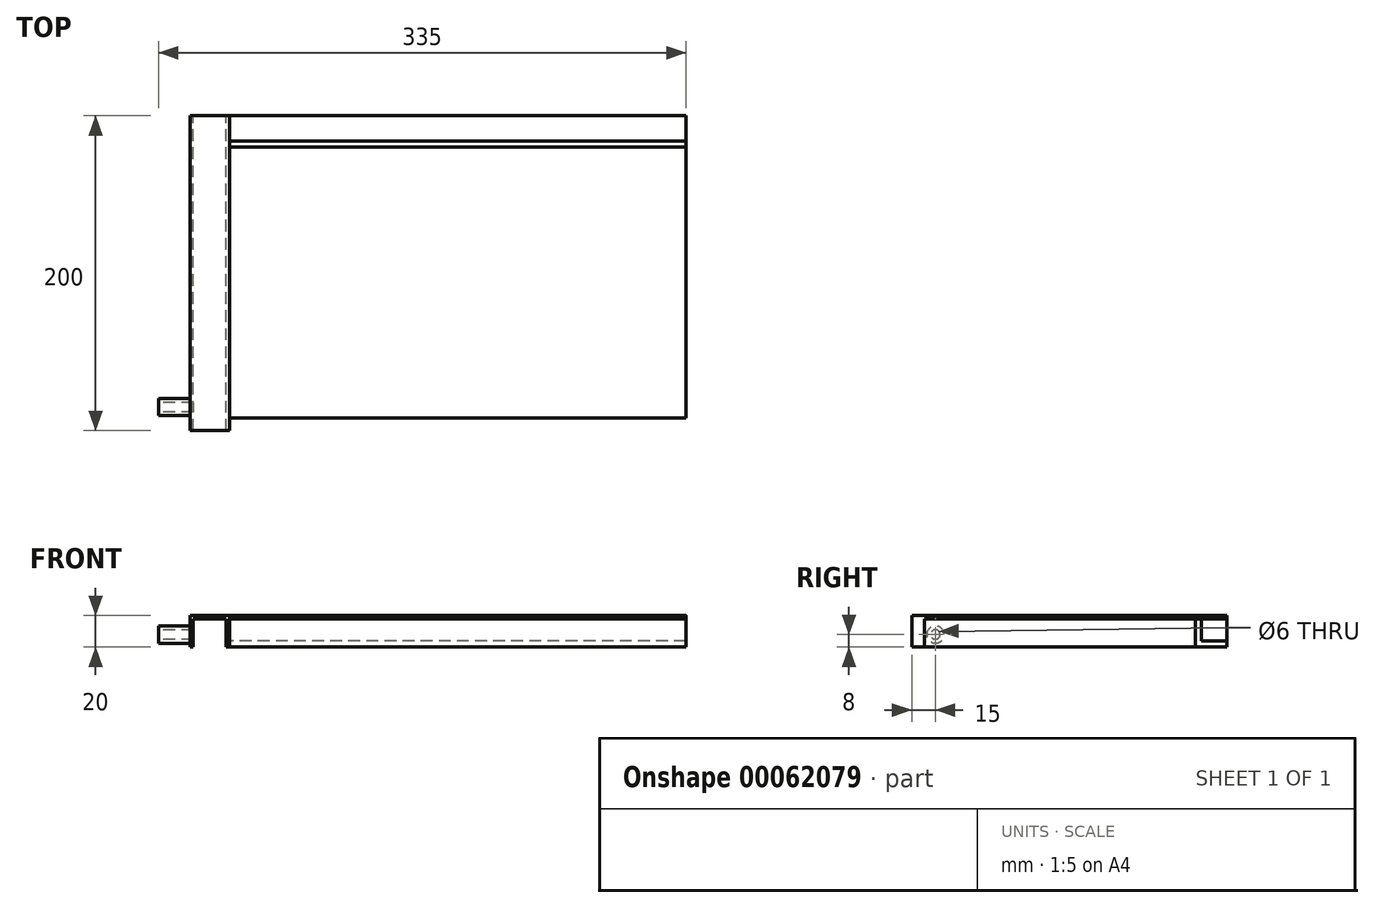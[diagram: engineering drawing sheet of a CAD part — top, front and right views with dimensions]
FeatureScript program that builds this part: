
annotation { "Feature Type Name" : "Feature", "Feature Type Description" : "" }
export const myFeature = defineFeature(function(context is Context, id is Id, definition is map)
    precondition{}
    {
        {
            assignVariable(context, id + "F0", {"name" : "l", "anyValue" : 200});
        }
        {
            assignVariable(context, id + "F1", {"name" : "w", "anyValue" : 294});
        }
        {
            var Q0;
            Q0=qCreatedBy(makeId("Front.planeOp"),FACE);
            var sketch = newSketch(context, id + "F2", { "sketchPlane" : qUnion([Q0])});
            skLineSegment(sketch, "E0.bottom", {"start": v(0, 0) * mm, "end": v(-2, 0) * mm});
            skLineSegment(sketch, "E0.top", {"start": v(0, 20) * mm, "end": v(-25, 20) * mm});
            skLineSegment(sketch, "E0.left", {"start": v(0, 0) * mm, "end": v(0, 20) * mm});
            skLineSegment(sketch, "E0.right", {"start": v(-25, 0) * mm, "end": v(-25, 20) * mm});
            skLineSegment(sketch, "E1.top", {"start": v(-2, 18) * mm, "end": v(-23, 18) * mm});
            skLineSegment(sketch, "E1.left", {"start": v(-2, 0) * mm, "end": v(-2, 18) * mm});
            skLineSegment(sketch, "E1.right", {"start": v(-23, 0) * mm, "end": v(-23, 18) * mm});
            skLineSegment(sketch, "E2", {"start": v(-23, 0) * mm, "end": v(-25, 0) * mm});
            skLineSegment(sketch, "E3", {"start": v(-23, 18) * mm, "end": v(-23, 20) * mm, "construction": true});
            skSolve(sketch);
        }
        {
            var Q0;
            Q0=makeQuery(id+"F2.imprint","IMPRINT",FACE,{"disambiguationData":[TD([[makeQuery(id+"F2.imprint","IMPRINT",EDGE,{"derivedFrom":sQuery(id+"F2.wireOp",EDGE,"E0.bottom")}),-1.0]])]});
            extrude(context, id + "F3", {"entities" : qUnion([Q0]), "depth" : (getVariable(context, 'l')) * mm});
        }
        {
            var Q0;
            Q0 = qSketchRegion(id + "F2", true);
            extrude(context, id + "F4", {"entities" : qUnion([Q0]), "depth" : (getVariable(context, 'l')) * mm});
        }
        {
            var Q0;
            Q0=makeQuery(id+"F4.opExtrude","SWEPT_FACE",FACE,{"disambiguationData":[OSD([sQuery(id+"F2.wireOp",EDGE,"E0.right")])]});
            var sketch = newSketch(context, id + "F5", { "sketchPlane" : qUnion([Q0])});
            skCircle(sketch, "E4", {"center": v(185, 8) * mm, "radius": 5.5 * mm});
            skSolve(sketch);
        }
        {
            var Q0;
            Q0=makeQuery(id+"F5.imprint","IMPRINT",FACE,{"disambiguationData":[TD([[makeQuery(id+"F5.imprint","IMPRINT",EDGE,{"derivedFrom":sQuery(id+"F5.wireOp",EDGE,"E4")}),1.0]])]});
            extrude(context, id + "F6", {"entities" : qUnion([Q0]), "operationType" : NewBodyOperationType.ADD, "depth" : 20 * mm});
        }
        {
            var Q0;
            Q0=makeQuery(id+"F6.opExtrude","CAP_FACE",FACE,{"disambiguationData":[OSD([sQuery(id+"F5.wireOp",EDGE,"E4")])],"isStart":false});
            var sketch = newSketch(context, id + "F7", { "sketchPlane" : qUnion([Q0])});
            skCircle(sketch, "E5", {"center": v(185, 8) * mm, "radius": 3 * mm});
            skSolve(sketch);
        }
        {
            var Q0;
            Q0=makeQuery(id+"F7.imprint","IMPRINT",FACE,{"disambiguationData":[TD([[makeQuery(id+"F7.imprint","IMPRINT",EDGE,{"derivedFrom":sQuery(id+"F7.wireOp",EDGE,"E5")}),1.0]])]});
            extrude(context, id + "F8", {"entities" : qUnion([Q0]), "operationType" : NewBodyOperationType.REMOVE, "oppositeDirection" : true, "depth" : 35 * mm});
        }
        {
            var Q0;
            Q0=qCreatedBy(makeId("Right.planeOp"),FACE);
            var sketch = newSketch(context, id + "F9", { "sketchPlane" : qUnion([Q0])});
            skLineSegment(sketch, "E6.bottom", {"start": v(0, 0) * mm, "end": v(-20, 0) * mm});
            skLineSegment(sketch, "E6.right", {"start": v(-20, 0) * mm, "end": v(-20, 20) * mm});
            skLineSegment(sketch, "E7.top", {"start": v(0, 4) * mm, "end": v(-16, 4) * mm});
            skLineSegment(sketch, "E7.right", {"start": v(-16, 20) * mm, "end": v(-16, 4) * mm});
            skLineSegment(sketch, "E8", {"start": v(-16, 20) * mm, "end": v(-20, 20) * mm});
            skLineSegment(sketch, "E9", {"start": v(0, 4) * mm, "end": v(0, 4) * mm});
            skLineSegment(sketch, "E10", {"start": v(0, 0) * mm, "end": v(0, 4) * mm});
            skSolve(sketch);
        }
        {
            var Q0;
            Q0=makeQuery(id+"F9.imprint","IMPRINT",FACE,{"disambiguationData":[TD([[makeQuery(id+"F9.imprint","IMPRINT",EDGE,{"derivedFrom":sQuery(id+"F9.wireOp",EDGE,"E6.bottom")}),-1.0]])]});
            extrude(context, id + "F10", {"entities" : qUnion([Q0]), "depth" : (getVariable(context, 'w') - 4) * mm});
        }
        {
            var Q0;
            Q0=makeQuery(id+"F10.opExtrude","SWEPT_EDGE",EDGE,{"disambiguationData":[OSD([sQuery(id+"F9.wireOp",EDGE,"E7.right"),sQuery(id+"F9.wireOp",EDGE,"E8")])]});
            var Q1;
            Q1=makeQuery(id+"F10.opExtrude","SWEPT_EDGE",EDGE,{"disambiguationData":[OSD([sQuery(id+"F9.wireOp",EDGE,"E7.top"),sQuery(id+"F9.wireOp",EDGE,"E10")])]});
            var Q2;
            Q2=makeQuery(id+"F10.opExtrude","SWEPT_EDGE",EDGE,{"disambiguationData":[OSD([sQuery(id+"F9.wireOp",EDGE,"E6.bottom"),sQuery(id+"F9.wireOp",EDGE,"E10")])]});
            var Q3;
            Q3=makeQuery(id+"F10.opExtrude","SWEPT_EDGE",EDGE,{"disambiguationData":[OSD([sQuery(id+"F9.wireOp",EDGE,"E6.bottom"),sQuery(id+"F9.wireOp",EDGE,"E6.right")])]});
            var Q4;
            Q4=makeQuery(id+"F10.opExtrude","SWEPT_EDGE",EDGE,{"disambiguationData":[OSD([sQuery(id+"F9.wireOp",EDGE,"E6.right"),sQuery(id+"F9.wireOp",EDGE,"E8")])]});
            fillet(context, id + "F11", {"entities" : qUnion([Q0, Q1, Q2, Q3, Q4]), "radius" : 1.5 * mm, "tangentPropagation" : true, "allowEdgeOverflow" : false});
        }
        {
            var Q0;
            Q0=qCreatedBy(makeId("Top.planeOp"),FACE);
            var sketch = newSketch(context, id + "F12", { "sketchPlane" : qUnion([Q0])});
            skLineSegment(sketch, "E11.bottom", {"start": v(0, 0) * mm, "end": v(290, 0) * mm});
            skLineSegment(sketch, "E11.top", {"start": v(0, -192) * mm, "end": v(290, -192) * mm});
            skLineSegment(sketch, "E11.left", {"start": v(0, 0) * mm, "end": v(0, -192) * mm});
            skLineSegment(sketch, "E11.right", {"start": v(290, 0) * mm, "end": v(290, -192) * mm});
            skSolve(sketch);
        }
        {
            var Q0;
            Q0=makeQuery(id+"F12.imprint","IMPRINT",FACE,{"disambiguationData":[TD([[makeQuery(id+"F12.imprint","IMPRINT",EDGE,{"derivedFrom":sQuery(id+"F12.wireOp",EDGE,"E11.bottom")}),-1.0]])]});
            extrude(context, id + "F13", {"entities" : qUnion([Q0]), "depth" : 18 * mm});
        }
    });
